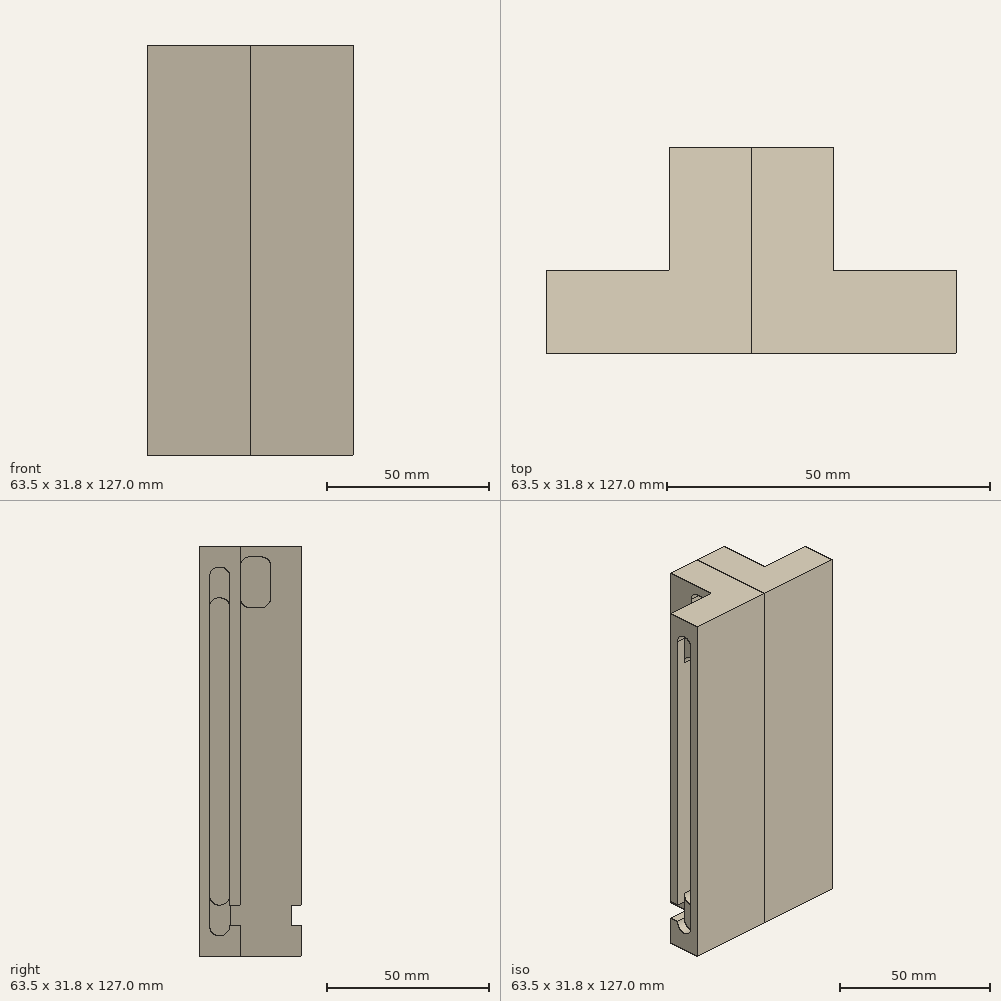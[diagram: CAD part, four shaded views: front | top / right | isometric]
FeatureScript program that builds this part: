
annotation { "Feature Type Name" : "Feature", "Feature Type Description" : "" }
export const myFeature = defineFeature(function(context is Context, id is Id, definition is map)
    precondition{}
    {
        {
            var Q0;
            Q0=qCreatedBy(makeId("Top.planeOp"),FACE);
            var sketch = newSketch(context, id + "F0", { "sketchPlane" : qUnion([Q0])});
            skLineSegment(sketch, "E0.bottom", {"start": v(0, 0) * mm, "end": v(31.75, 0) * mm});
            skLineSegment(sketch, "E0.left", {"start": v(0, 0) * mm, "end": v(0, 31.75) * mm});
            skLineSegment(sketch, "E1", {"start": v(0, 31.75) * mm, "end": v(12.7, 31.75) * mm});
            skLineSegment(sketch, "E2", {"start": v(12.7, 31.75) * mm, "end": v(12.7, 12.7) * mm});
            skLineSegment(sketch, "E3", {"start": v(12.7, 12.7) * mm, "end": v(31.75, 12.7) * mm});
            skLineSegment(sketch, "E4", {"start": v(31.75, 12.7) * mm, "end": v(31.75, 0) * mm});
            skSolve(sketch);
        }
        {
            var Q0;
            Q0=makeQuery(id+"F0.imprint","IMPRINT",FACE,{"disambiguationData":[TD([[makeQuery(id+"F0.imprint","IMPRINT",EDGE,{"derivedFrom":sQuery(id+"F0.wireOp",EDGE,"E0.bottom")}),1.0]])]});
            extrude(context, id + "F1", {"entities" : qUnion([Q0]), "depth" : 127 * mm});
        }
        {
            var Q0;
            Q0=makeQuery(id+"F1.opExtrude","SWEPT_FACE",FACE,{"disambiguationData":[OSD([sQuery(id+"F0.wireOp",EDGE,"E4")])]});
            var sketch = newSketch(context, id + "F2", { "sketchPlane" : qUnion([Q0])});
            skLineSegment(sketch, "E5.bottom", {"start": v(6.35, 111.12) * mm, "end": v(6.35, 111.12) * mm});
            skLineSegment(sketch, "E5.top", {"start": v(6.35, 15.88) * mm, "end": v(6.35, 15.88) * mm});
            skLineSegment(sketch, "E5.left", {"start": v(3.17, 107.95) * mm, "end": v(3.18, 19.05) * mm});
            skLineSegment(sketch, "E5.right", {"start": v(9.52, 107.95) * mm, "end": v(9.53, 19.05) * mm});
            skPoint(sketch, "E6.visualSharp", {"position": v(3.17, 111.12) * mm});
            skArc(sketch, "E6.filletArc", {"start": v(6.35, 111.12) * mm, "mid": v(4.1, 110.2) * mm, "end": v(3.18, 107.95) * mm});
            skPoint(sketch, "E7.visualSharp", {"position": v(3.18, 15.88) * mm});
            skArc(sketch, "E7.filletArc", {"start": v(3.18, 19.05) * mm, "mid": v(4.1, 16.8) * mm, "end": v(6.35, 15.88) * mm});
            skPoint(sketch, "E8.visualSharp", {"position": v(9.53, 15.88) * mm});
            skArc(sketch, "E8.filletArc", {"start": v(6.35, 15.88) * mm, "mid": v(8.6, 16.8) * mm, "end": v(9.52, 19.05) * mm});
            skPoint(sketch, "E9.visualSharp", {"position": v(9.52, 111.12) * mm});
            skArc(sketch, "E9.filletArc", {"start": v(9.52, 107.95) * mm, "mid": v(8.6, 110.2) * mm, "end": v(6.35, 111.12) * mm});
            skSolve(sketch);
        }
        {
            var Q0;
            Q0 = qSketchRegion(id + "F2", true);
            var Q1;
            Q1=makeQuery(id+"F1.opExtrude","SWEPT_FACE",FACE,{"disambiguationData":[OSD([sQuery(id+"F0.wireOp",EDGE,"E2")])]});
            extrude(context, id + "F3", {"entities" : qUnion([Q0]), "operationType" : NewBodyOperationType.REMOVE, "endBound" : BoundingType.UP_TO_SURFACE, "oppositeDirection" : true, "endBoundEntityFace" : qUnion([Q1]), "depth" : 19.05 * mm});
        }
        {
            var Q0;
            Q0=makeQuery(id+"F1.opExtrude","SWEPT_FACE",FACE,{"disambiguationData":[OSD([sQuery(id+"F0.wireOp",EDGE,"E3")])]});
            var sketch = newSketch(context, id + "F4", { "sketchPlane" : qUnion([Q0])});
            skLineSegment(sketch, "E10.bottom", {"start": v(-19.05, 123.83) * mm, "end": v(-15.87, 123.83) * mm});
            skLineSegment(sketch, "E10.top", {"start": v(-19.05, 107.95) * mm, "end": v(-15.87, 107.95) * mm});
            skLineSegment(sketch, "E10.left", {"start": v(-22.23, 120.65) * mm, "end": v(-22.23, 111.12) * mm});
            skLineSegment(sketch, "E10.right", {"start": v(-12.7, 120.65) * mm, "end": v(-12.7, 111.12) * mm});
            skLineSegment(sketch, "E11.bottom", {"start": v(-15.87, 3.18) * mm, "end": v(-19.05, 3.18) * mm});
            skLineSegment(sketch, "E11.left", {"start": v(-12.7, 6.35) * mm, "end": v(-12.7, 15.88) * mm});
            skPoint(sketch, "E12.visualSharp", {"position": v(-12.7, 123.83) * mm});
            skArc(sketch, "E12.filletArc", {"start": v(-12.7, 120.65) * mm, "mid": v(-13.63, 122.9) * mm, "end": v(-15.87, 123.83) * mm});
            skPoint(sketch, "E13.visualSharp", {"position": v(-22.23, 123.83) * mm});
            skArc(sketch, "E13.filletArc", {"start": v(-19.05, 123.83) * mm, "mid": v(-21.3, 122.9) * mm, "end": v(-22.23, 120.65) * mm});
            skPoint(sketch, "E14.visualSharp", {"position": v(-22.23, 107.95) * mm});
            skArc(sketch, "E14.filletArc", {"start": v(-22.23, 111.12) * mm, "mid": v(-21.3, 108.88) * mm, "end": v(-19.05, 107.95) * mm});
            skPoint(sketch, "E15.visualSharp", {"position": v(-12.7, 107.95) * mm});
            skArc(sketch, "E15.filletArc", {"start": v(-15.87, 107.95) * mm, "mid": v(-13.63, 108.88) * mm, "end": v(-12.7, 111.12) * mm});
            skPoint(sketch, "E16.visualSharp", {"position": v(-12.7, 15.88) * mm});
            skArc(sketch, "E16.filletArc", {"start": v(-12.7, 15.88) * mm, "mid": v(-13.63, 18.12) * mm, "end": v(-15.87, 19.05) * mm});
            skPoint(sketch, "E17.visualSharp", {"position": v(-22.23, 3.18) * mm});
            skArc(sketch, "E17.filletArc", {"start": v(-22.23, 6.35) * mm, "mid": v(-21.3, 4.1) * mm, "end": v(-19.05, 3.18) * mm});
            skPoint(sketch, "E18.visualSharp", {"position": v(-12.7, 3.17) * mm});
            skArc(sketch, "E18.filletArc", {"start": v(-15.87, 3.18) * mm, "mid": v(-13.63, 4.1) * mm, "end": v(-12.7, 6.35) * mm});
            skLineSegment(sketch, "E19", {"start": v(-15.87, 19.05) * mm, "end": v(-19.05, 19.05) * mm});
            skLineSegment(sketch, "E20", {"start": v(-22.23, 6.35) * mm, "end": v(-22.23, 15.88) * mm});
            skArc(sketch, "E21", {"start": v(-22.22, 15.88) * mm, "mid": v(-21.3, 18.12) * mm, "end": v(-19.05, 19.05) * mm});
            skSolve(sketch);
        }
        {
            var Q0;
            Q0=makeQuery(id+"F4.imprint","IMPRINT",FACE,{"disambiguationData":[TD([[makeQuery(id+"F4.imprint","IMPRINT",EDGE,{"derivedFrom":sQuery(id+"F4.wireOp",EDGE,"E10.bottom")}),-1.0]])]});
            var Q1;
            Q1=makeQuery(id+"F4.imprint","IMPRINT",FACE,{"disambiguationData":[TD([[makeQuery(id+"F4.imprint","IMPRINT",EDGE,{"derivedFrom":sQuery(id+"F4.wireOp",EDGE,"E11.bottom")}),-1.0]])]});
            extrude(context, id + "F5", {"entities" : qUnion([Q0, Q1]), "operationType" : NewBodyOperationType.REMOVE, "oppositeDirection" : true, "depth" : 9.52 * mm});
        }
        {
            var Q0;
            Q0=makeQuery(id+"F1.opExtrude","SWEPT_FACE",FACE,{"disambiguationData":[OSD([sQuery(id+"F0.wireOp",EDGE,"E4")])]});
            var sketch = newSketch(context, id + "F6", { "sketchPlane" : qUnion([Q0])});
            skLineSegment(sketch, "E22.bottom", {"start": v(6.35, 120.65) * mm, "end": v(6.35, 120.65) * mm});
            skLineSegment(sketch, "E22.top", {"start": v(6.35, 6.35) * mm, "end": v(6.35, 6.35) * mm});
            skLineSegment(sketch, "E22.left", {"start": v(3.17, 117.48) * mm, "end": v(3.18, 9.52) * mm});
            skLineSegment(sketch, "E22.right", {"start": v(9.52, 117.48) * mm, "end": v(9.53, 9.52) * mm});
            skPoint(sketch, "E23.visualSharp", {"position": v(9.52, 120.65) * mm});
            skArc(sketch, "E23.filletArc", {"start": v(9.52, 117.48) * mm, "mid": v(8.6, 119.72) * mm, "end": v(6.35, 120.65) * mm});
            skPoint(sketch, "E24.visualSharp", {"position": v(3.17, 120.65) * mm});
            skArc(sketch, "E24.filletArc", {"start": v(6.35, 120.65) * mm, "mid": v(4.1, 119.72) * mm, "end": v(3.17, 117.48) * mm});
            skPoint(sketch, "E25.visualSharp", {"position": v(3.18, 6.35) * mm});
            skArc(sketch, "E25.filletArc", {"start": v(3.18, 9.52) * mm, "mid": v(4.1, 7.28) * mm, "end": v(6.35, 6.35) * mm});
            skPoint(sketch, "E26.visualSharp", {"position": v(9.53, 6.35) * mm});
            skArc(sketch, "E26.filletArc", {"start": v(6.35, 6.35) * mm, "mid": v(8.6, 7.28) * mm, "end": v(9.53, 9.52) * mm});
            skSolve(sketch);
        }
        {
            var Q0;
            Q0 = qSketchRegion(id + "F6", true);
            extrude(context, id + "F7", {"entities" : qUnion([Q0]), "operationType" : NewBodyOperationType.REMOVE, "oppositeDirection" : true, "depth" : 3.17 * mm});
        }
        {
            var Q0;
            Q0=makeQuery(id+"F1.opExtrude","SWEPT_FACE",FACE,{"disambiguationData":[OSD([sQuery(id+"F0.wireOp",EDGE,"E1")])]});
            var sketch = newSketch(context, id + "F8", { "sketchPlane" : qUnion([Q0])});
            skLineSegment(sketch, "E27.bottom", {"start": v(-6.35, 120.65) * mm, "end": v(-6.35, 120.65) * mm});
            skLineSegment(sketch, "E27.left", {"start": v(-9.53, 117.48) * mm, "end": v(-9.52, 15.88) * mm});
            skLineSegment(sketch, "E27.right", {"start": v(-3.18, 117.48) * mm, "end": v(-3.17, 15.88) * mm});
            skPoint(sketch, "E28.visualSharp", {"position": v(-9.53, 120.65) * mm});
            skArc(sketch, "E28.filletArc", {"start": v(-6.35, 120.65) * mm, "mid": v(-8.6, 119.72) * mm, "end": v(-9.53, 117.48) * mm});
            skPoint(sketch, "E29.visualSharp", {"position": v(-3.18, 120.65) * mm});
            skArc(sketch, "E29.filletArc", {"start": v(-3.18, 117.48) * mm, "mid": v(-4.1, 119.72) * mm, "end": v(-6.35, 120.65) * mm});
            skLineSegment(sketch, "E30", {"start": v(-3.17, 15.88) * mm, "end": v(0, 15.88) * mm});
            skLineSegment(sketch, "E31", {"start": v(0, 15.88) * mm, "end": v(0, 9.53) * mm});
            skLineSegment(sketch, "E32", {"start": v(0, 9.53) * mm, "end": v(-12.7, 9.52) * mm});
            skLineSegment(sketch, "E33", {"start": v(-12.7, 9.53) * mm, "end": v(-12.7, 15.88) * mm});
            skLineSegment(sketch, "E34", {"start": v(-12.7, 15.88) * mm, "end": v(-9.53, 15.88) * mm});
            skSolve(sketch);
        }
        {
            var Q0;
            Q0 = qSketchRegion(id + "F8", true);
            extrude(context, id + "F9", {"entities" : qUnion([Q0]), "operationType" : NewBodyOperationType.REMOVE, "oppositeDirection" : true, "depth" : 3.17 * mm});
        }
        {
            var Q0;
            Q0=makeQuery(id+"F1.opExtrude","SWEPT_FACE",FACE,{"disambiguationData":[OSD([sQuery(id+"F0.wireOp",EDGE,"E1")])]});
            var sketch = newSketch(context, id + "F10", { "sketchPlane" : qUnion([Q0])});
            skLineSegment(sketch, "E35.bottom", {"start": v(-6.35, 111.12) * mm, "end": v(-6.35, 111.12) * mm});
            skLineSegment(sketch, "E35.top", {"start": v(-6.35, 73.03) * mm, "end": v(-6.35, 73.03) * mm});
            skLineSegment(sketch, "E35.left", {"start": v(-9.53, 107.95) * mm, "end": v(-9.53, 76.2) * mm});
            skLineSegment(sketch, "E35.right", {"start": v(-3.17, 107.95) * mm, "end": v(-3.17, 76.2) * mm});
            skPoint(sketch, "E36.visualSharp", {"position": v(-9.53, 73.03) * mm});
            skArc(sketch, "E36.filletArc", {"start": v(-9.52, 76.2) * mm, "mid": v(-8.6, 73.95) * mm, "end": v(-6.35, 73.03) * mm});
            skPoint(sketch, "E37.visualSharp", {"position": v(-3.18, 73.03) * mm});
            skArc(sketch, "E37.filletArc", {"start": v(-6.35, 73.03) * mm, "mid": v(-4.1, 73.95) * mm, "end": v(-3.18, 76.2) * mm});
            skPoint(sketch, "E38.visualSharp", {"position": v(-3.18, 111.12) * mm});
            skArc(sketch, "E38.filletArc", {"start": v(-3.18, 107.95) * mm, "mid": v(-4.1, 110.2) * mm, "end": v(-6.35, 111.12) * mm});
            skPoint(sketch, "E39.visualSharp", {"position": v(-9.53, 111.12) * mm});
            skArc(sketch, "E39.filletArc", {"start": v(-6.35, 111.12) * mm, "mid": v(-8.6, 110.2) * mm, "end": v(-9.52, 107.95) * mm});
            skSolve(sketch);
        }
        {
            var Q0;
            Q0 = qSketchRegion(id + "F10", true);
            var Q1;
            Q1=makeQuery(id+"F1.opExtrude","SWEPT_FACE",FACE,{"disambiguationData":[OSD([sQuery(id+"F0.wireOp",EDGE,"E3")])]});
            extrude(context, id + "F11", {"entities" : qUnion([Q0]), "operationType" : NewBodyOperationType.REMOVE, "endBound" : BoundingType.UP_TO_SURFACE, "oppositeDirection" : true, "endBoundEntityFace" : qUnion([Q1]), "depth" : 19.05 * mm});
        }
        {
            var Q0;
            {var subQ0=sQuery(id+"F0.wireOp",EDGE,"E2");Q0=makeQuery(id+"F5.boolean.opBoolean","MERGE",FACE,{"derivedFrom":[makeQuery(id+"F1.opExtrude","SWEPT_FACE",FACE,{"disambiguationData":[OSD([subQ0])]}),makeQuery(id+"F3.boolean.opBoolean","COPY",FACE,{"derivedFrom":makeQuery(id+"F3.opExtrude","CAP_FACE",FACE,{"disambiguationData":[OSD([subQ0])],"isStart":false})}),makeQuery(id+"F5.opExtrude","SWEPT_FACE",FACE,{"disambiguationData":[OSD([sQuery(id+"F4.wireOp",EDGE,"E10.right")])]}),makeQuery(id+"F5.opExtrude","SWEPT_FACE",FACE,{"disambiguationData":[OSD([sQuery(id+"F4.wireOp",EDGE,"E11.left")])]})]});}
            var sketch = newSketch(context, id + "F12", { "sketchPlane" : qUnion([Q0])});
            skLineSegment(sketch, "E40.bottom", {"start": v(19.05, 123.83) * mm, "end": v(15.87, 123.83) * mm});
            skLineSegment(sketch, "E40.top", {"start": v(19.05, 107.95) * mm, "end": v(15.87, 107.95) * mm});
            skLineSegment(sketch, "E40.left", {"start": v(22.22, 120.65) * mm, "end": v(22.23, 111.12) * mm});
            skLineSegment(sketch, "E40.right", {"start": v(12.7, 120.65) * mm, "end": v(12.7, 111.12) * mm});
            skPoint(sketch, "E41.visualSharp", {"position": v(22.22, 107.95) * mm});
            skArc(sketch, "E41.filletArc", {"start": v(19.05, 107.95) * mm, "mid": v(21.3, 108.88) * mm, "end": v(22.23, 111.12) * mm});
            skPoint(sketch, "E42.visualSharp", {"position": v(22.22, 123.83) * mm});
            skArc(sketch, "E42.filletArc", {"start": v(22.23, 120.65) * mm, "mid": v(21.3, 122.9) * mm, "end": v(19.05, 123.83) * mm});
            skPoint(sketch, "E43.visualSharp", {"position": v(12.7, 123.83) * mm});
            skArc(sketch, "E43.filletArc", {"start": v(15.87, 123.83) * mm, "mid": v(13.63, 122.9) * mm, "end": v(12.7, 120.65) * mm});
            skPoint(sketch, "E44.visualSharp", {"position": v(12.7, 107.95) * mm});
            skArc(sketch, "E44.filletArc", {"start": v(12.7, 111.12) * mm, "mid": v(13.63, 108.88) * mm, "end": v(15.87, 107.95) * mm});
            skSolve(sketch);
        }
        {
            var Q0;
            Q0 = qSketchRegion(id + "F12", true);
            var Q1;
            Q1=makeQuery(id+"F11.boolean.opBoolean","MERGE",FACE,{"derivedFrom":[makeQuery(id+"F9.boolean.opBoolean","COPY",FACE,{"derivedFrom":makeQuery(id+"F9.opExtrude","SWEPT_FACE",FACE,{"disambiguationData":[OSD([sQuery(id+"F8.wireOp",EDGE,"E27.right")])]})}),makeQuery(id+"F11.opExtrude","SWEPT_FACE",FACE,{"disambiguationData":[OSD([sQuery(id+"F10.wireOp",EDGE,"E35.right")])]})]});
            extrude(context, id + "F13", {"entities" : qUnion([Q0]), "operationType" : NewBodyOperationType.REMOVE, "endBound" : BoundingType.UP_TO_SURFACE, "oppositeDirection" : true, "endBoundEntityFace" : qUnion([Q1]), "depth" : 9.52 * mm});
        }
        {
            var Q0;
            Q0=makeQuery(id+"F1.opExtrude","SWEPT_FACE",FACE,{"disambiguationData":[OSD([sQuery(id+"F0.wireOp",EDGE,"E3")])]});
            var sketch = newSketch(context, id + "F14", { "sketchPlane" : qUnion([Q0])});
            skLineSegment(sketch, "E45.bottom", {"start": v(-22.23, 15.88) * mm, "end": v(-31.75, 15.88) * mm});
            skLineSegment(sketch, "E45.top", {"start": v(-22.23, 9.53) * mm, "end": v(-31.75, 9.53) * mm});
            skLineSegment(sketch, "E45.left", {"start": v(-22.23, 15.88) * mm, "end": v(-22.23, 9.53) * mm});
            skLineSegment(sketch, "E45.right", {"start": v(-31.75, 15.88) * mm, "end": v(-31.75, 9.53) * mm});
            skSolve(sketch);
        }
        {
            var Q0;
            Q0 = qSketchRegion(id + "F14", true);
            extrude(context, id + "F15", {"entities" : qUnion([Q0]), "operationType" : NewBodyOperationType.REMOVE, "oppositeDirection" : true, "depth" : 3.17 * mm});
        }
        {
            var Q0;
            Q0=makeQuery(id+"F1.opExtrude","SWEPT_BODY",BODY,{"disambiguationData":[OSD([sQuery(id+"F0.wireOp",EDGE,"E0.bottom"),sQuery(id+"F0.wireOp",EDGE,"E0.left"),sQuery(id+"F0.wireOp",EDGE,"E1"),sQuery(id+"F0.wireOp",EDGE,"E2"),sQuery(id+"F0.wireOp",EDGE,"E3"),sQuery(id+"F0.wireOp",EDGE,"E4")])]});
            var Q1;
            Q1=qCreatedBy(makeId("Right.planeOp"),FACE);
            mirror(context, id + "F16", {"entities" : qUnion([Q0]), "mirrorPlane" : qUnion([Q1])});
        }
    });
